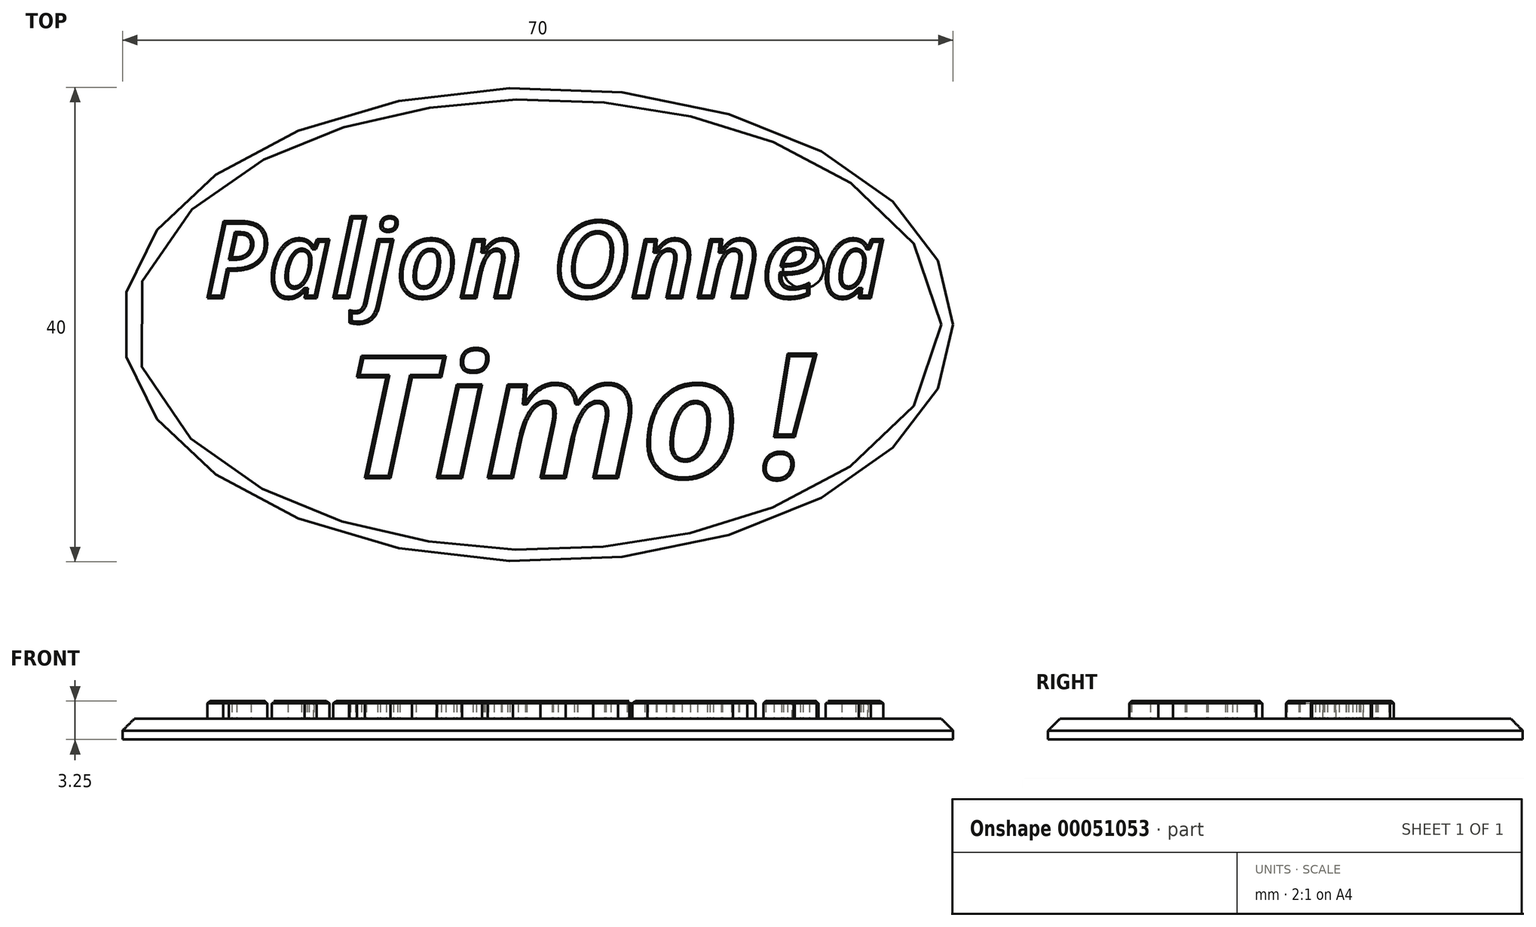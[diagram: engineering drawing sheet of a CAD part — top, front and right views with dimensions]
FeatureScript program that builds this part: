
annotation { "Feature Type Name" : "Feature", "Feature Type Description" : "" }
export const myFeature = defineFeature(function(context is Context, id is Id, definition is map)
    precondition{}
    {
        {
            var Q0;
            Q0=qCreatedBy(makeId("Top.planeOp"),FACE);
            var sketch = newSketch(context, id + "F0", { "sketchPlane" : qUnion([Q0])});
            skEllipse(sketch, "E0", {"center": v(0, 0) * mm, "majorRadius": 35 * mm, "minorRadius": 20 * mm, "majorAxis": v(1, 0)});
            skSolve(sketch);
        }
        {
            var Q0;
            Q0=makeQuery(id+"F0.imprint","IMPRINT",FACE,{"disambiguationData":[TD([[makeQuery(id+"F0.imprint","IMPRINT",EDGE,{"derivedFrom":sQuery(id+"F0.wireOp",EDGE,"E0")}),1.0]])]});
            extrude(context, id + "F1", {"entities" : qUnion([Q0]), "depth" : 1.75 * mm});
        }
        {
            var Q0;
            Q0=makeQuery(id+"F1.opExtrude","CAP_FACE",FACE,{"disambiguationData":[OSD([sQuery(id+"F0.wireOp",EDGE,"E0")])],"isStart":false});
            var sketch = newSketch(context, id + "F2", { "sketchPlane" : qUnion([Q0])});
            skText(sketch, "E1", { "text": "Paljon Onnea ", "fontName": "OpenSans-BoldItalic.ttf"});
            const initialGuessF2  = {"E1": [-0.0281, 0.00223, 1, 0, 0.00655]};
            skSetInitialGuess(sketch, initialGuessF2);
            skSolve(sketch);
        }
        {
            var Q0;
            Q0=makeQuery(id+"F2.imprint","IMPRINT",FACE,{"disambiguationData":[TD([[makeQuery(id+"F2.imprint","IMPRINT",EDGE,{"derivedFrom":sQuery(id+"F2.wireOp",EDGE,"E1.sketch_text.stroke-6")}),1.0]])]});
            var sketch = newSketch(context, id + "F3", { "sketchPlane" : qUnion([Q0])});
            skText(sketch, "E2", { "text": "Timo", "fontName": "OpenSans-BoldItalic.ttf"});
            const initialGuessF3  = {"E2": [-0.01644, -0.01295, 1, 0, 0.01041]};
            skSetInitialGuess(sketch, initialGuessF3);
            skSolve(sketch);
        }
        {
            var Q0;
            Q0 = qSketchRegion(id + "F2", true);
            var Q1;
            Q1 = qSketchRegion(id + "F3", true);
            extrude(context, id + "F4", {"entities" : qUnion([Q0, Q1]), "operationType" : NewBodyOperationType.ADD, "depth" : 1.5 * mm});
        }
        {
            var Q0;
            Q0=makeQuery(id+"F4.opExtrude","CAP_FACE",FACE,{"disambiguationData":[OSD([sQuery(id+"F3.wireOp",EDGE,"E2.sketch_text.stroke-0"),sQuery(id+"F3.wireOp",EDGE,"E2.sketch_text.stroke-1"),sQuery(id+"F3.wireOp",EDGE,"E2.sketch_text.stroke-2"),sQuery(id+"F3.wireOp",EDGE,"E2.sketch_text.stroke-3"),sQuery(id+"F3.wireOp",EDGE,"E2.sketch_text.stroke-4"),sQuery(id+"F3.wireOp",EDGE,"E2.sketch_text.stroke-5"),sQuery(id+"F3.wireOp",EDGE,"E2.sketch_text.stroke-6"),sQuery(id+"F3.wireOp",EDGE,"E2.sketch_text.stroke-7")])],"isStart":false});
            var Q1;
            Q1=makeQuery(id+"F4.opExtrude","CAP_FACE",FACE,{"disambiguationData":[OSD([sQuery(id+"F3.wireOp",EDGE,"E2.sketch_text.stroke-15"),sQuery(id+"F3.wireOp",EDGE,"E2.sketch_text.stroke-16"),sQuery(id+"F3.wireOp",EDGE,"E2.sketch_text.stroke-17"),sQuery(id+"F3.wireOp",EDGE,"E2.sketch_text.stroke-18")])],"isStart":false});
            var Q2;
            Q2=makeQuery(id+"F4.opExtrude","CAP_FACE",FACE,{"disambiguationData":[OSD([sQuery(id+"F3.wireOp",EDGE,"E2.sketch_text.stroke-8"),sQuery(id+"F3.wireOp",EDGE,"E2.sketch_text.stroke-9"),sQuery(id+"F3.wireOp",EDGE,"E2.sketch_text.stroke-10"),sQuery(id+"F3.wireOp",EDGE,"E2.sketch_text.stroke-11"),sQuery(id+"F3.wireOp",EDGE,"E2.sketch_text.stroke-12"),sQuery(id+"F3.wireOp",EDGE,"E2.sketch_text.stroke-13"),sQuery(id+"F3.wireOp",EDGE,"E2.sketch_text.stroke-14")])],"isStart":false});
            var Q3;
            Q3=makeQuery(id+"F4.opExtrude","CAP_FACE",FACE,{"disambiguationData":[OSD([sQuery(id+"F3.wireOp",EDGE,"E2.sketch_text.stroke-47"),sQuery(id+"F3.wireOp",EDGE,"E2.sketch_text.stroke-48"),sQuery(id+"F3.wireOp",EDGE,"E2.sketch_text.stroke-49"),sQuery(id+"F3.wireOp",EDGE,"E2.sketch_text.stroke-50"),sQuery(id+"F3.wireOp",EDGE,"E2.sketch_text.stroke-51"),sQuery(id+"F3.wireOp",EDGE,"E2.sketch_text.stroke-52"),sQuery(id+"F3.wireOp",EDGE,"E2.sketch_text.stroke-53"),sQuery(id+"F3.wireOp",EDGE,"E2.sketch_text.stroke-54"),sQuery(id+"F3.wireOp",EDGE,"E2.sketch_text.stroke-55"),sQuery(id+"F3.wireOp",EDGE,"E2.sketch_text.stroke-56"),sQuery(id+"F3.wireOp",EDGE,"E2.sketch_text.stroke-57"),sQuery(id+"F3.wireOp",EDGE,"E2.sketch_text.stroke-58"),sQuery(id+"F3.wireOp",EDGE,"E2.sketch_text.stroke-59"),sQuery(id+"F3.wireOp",EDGE,"E2.sketch_text.stroke-60"),sQuery(id+"F3.wireOp",EDGE,"E2.sketch_text.stroke-61"),sQuery(id+"F3.wireOp",EDGE,"E2.sketch_text.stroke-62"),sQuery(id+"F3.wireOp",EDGE,"E2.sketch_text.stroke-63"),sQuery(id+"F3.wireOp",EDGE,"E2.sketch_text.stroke-64")])],"isStart":false});
            var Q4;
            Q4=makeQuery(id+"F4.opExtrude","CAP_FACE",FACE,{"disambiguationData":[OSD([sQuery(id+"F2.wireOp",EDGE,"E1.sketch_text.stroke-94"),sQuery(id+"F2.wireOp",EDGE,"E1.sketch_text.stroke-95"),sQuery(id+"F2.wireOp",EDGE,"E1.sketch_text.stroke-96"),sQuery(id+"F2.wireOp",EDGE,"E1.sketch_text.stroke-97"),sQuery(id+"F2.wireOp",EDGE,"E1.sketch_text.stroke-98"),sQuery(id+"F2.wireOp",EDGE,"E1.sketch_text.stroke-99"),sQuery(id+"F2.wireOp",EDGE,"E1.sketch_text.stroke-100"),sQuery(id+"F2.wireOp",EDGE,"E1.sketch_text.stroke-101"),sQuery(id+"F2.wireOp",EDGE,"E1.sketch_text.stroke-102"),sQuery(id+"F2.wireOp",EDGE,"E1.sketch_text.stroke-103"),sQuery(id+"F2.wireOp",EDGE,"E1.sketch_text.stroke-104"),sQuery(id+"F2.wireOp",EDGE,"E1.sketch_text.stroke-105"),sQuery(id+"F2.wireOp",EDGE,"E1.sketch_text.stroke-106"),sQuery(id+"F2.wireOp",EDGE,"E1.sketch_text.stroke-107"),sQuery(id+"F2.wireOp",EDGE,"E1.sketch_text.stroke-108"),sQuery(id+"F2.wireOp",EDGE,"E1.sketch_text.stroke-109"),sQuery(id+"F2.wireOp",EDGE,"E1.sketch_text.stroke-110"),sQuery(id+"F2.wireOp",EDGE,"E1.sketch_text.stroke-111"),sQuery(id+"F2.wireOp",EDGE,"E1.sketch_text.stroke-112"),sQuery(id+"F2.wireOp",EDGE,"E1.sketch_text.stroke-113")])],"isStart":false});
            var Q5;
            Q5=makeQuery(id+"F4.opExtrude","CAP_FACE",FACE,{"disambiguationData":[OSD([sQuery(id+"F2.wireOp",EDGE,"E1.sketch_text.stroke-40"),sQuery(id+"F2.wireOp",EDGE,"E1.sketch_text.stroke-41"),sQuery(id+"F2.wireOp",EDGE,"E1.sketch_text.stroke-42"),sQuery(id+"F2.wireOp",EDGE,"E1.sketch_text.stroke-43")])],"isStart":false});
            chamfer(context, id + "F5", {"entities" : qUnion([Q0, Q1, Q2, Q3, Q4, Q5]), "width" : 0.2 * mm});
        }
        {
            var Q0;
            Q0=makeQuery(id+"F4.opExtrude","CAP_FACE",FACE,{"disambiguationData":[OSD([sQuery(id+"F2.wireOp",EDGE,"E1.sketch_text.stroke-0"),sQuery(id+"F2.wireOp",EDGE,"E1.sketch_text.stroke-1"),sQuery(id+"F2.wireOp",EDGE,"E1.sketch_text.stroke-2"),sQuery(id+"F2.wireOp",EDGE,"E1.sketch_text.stroke-3"),sQuery(id+"F2.wireOp",EDGE,"E1.sketch_text.stroke-4"),sQuery(id+"F2.wireOp",EDGE,"E1.sketch_text.stroke-5"),sQuery(id+"F2.wireOp",EDGE,"E1.sketch_text.stroke-6"),sQuery(id+"F2.wireOp",EDGE,"E1.sketch_text.stroke-7"),sQuery(id+"F2.wireOp",EDGE,"E1.sketch_text.stroke-8"),sQuery(id+"F2.wireOp",EDGE,"E1.sketch_text.stroke-9"),sQuery(id+"F2.wireOp",EDGE,"E1.sketch_text.stroke-10"),sQuery(id+"F2.wireOp",EDGE,"E1.sketch_text.stroke-11"),sQuery(id+"F2.wireOp",EDGE,"E1.sketch_text.stroke-12"),sQuery(id+"F2.wireOp",EDGE,"E1.sketch_text.stroke-13"),sQuery(id+"F2.wireOp",EDGE,"E1.sketch_text.stroke-14")])],"isStart":false});
            var Q1;
            Q1=makeQuery(id+"F4.opExtrude","CAP_FACE",FACE,{"disambiguationData":[OSD([sQuery(id+"F2.wireOp",EDGE,"E1.sketch_text.stroke-15"),sQuery(id+"F2.wireOp",EDGE,"E1.sketch_text.stroke-16"),sQuery(id+"F2.wireOp",EDGE,"E1.sketch_text.stroke-17"),sQuery(id+"F2.wireOp",EDGE,"E1.sketch_text.stroke-18"),sQuery(id+"F2.wireOp",EDGE,"E1.sketch_text.stroke-19"),sQuery(id+"F2.wireOp",EDGE,"E1.sketch_text.stroke-20"),sQuery(id+"F2.wireOp",EDGE,"E1.sketch_text.stroke-21"),sQuery(id+"F2.wireOp",EDGE,"E1.sketch_text.stroke-22"),sQuery(id+"F2.wireOp",EDGE,"E1.sketch_text.stroke-23"),sQuery(id+"F2.wireOp",EDGE,"E1.sketch_text.stroke-24"),sQuery(id+"F2.wireOp",EDGE,"E1.sketch_text.stroke-25"),sQuery(id+"F2.wireOp",EDGE,"E1.sketch_text.stroke-26"),sQuery(id+"F2.wireOp",EDGE,"E1.sketch_text.stroke-27"),sQuery(id+"F2.wireOp",EDGE,"E1.sketch_text.stroke-28"),sQuery(id+"F2.wireOp",EDGE,"E1.sketch_text.stroke-29"),sQuery(id+"F2.wireOp",EDGE,"E1.sketch_text.stroke-30"),sQuery(id+"F2.wireOp",EDGE,"E1.sketch_text.stroke-31"),sQuery(id+"F2.wireOp",EDGE,"E1.sketch_text.stroke-32"),sQuery(id+"F2.wireOp",EDGE,"E1.sketch_text.stroke-33"),sQuery(id+"F2.wireOp",EDGE,"E1.sketch_text.stroke-34"),sQuery(id+"F2.wireOp",EDGE,"E1.sketch_text.stroke-35"),sQuery(id+"F2.wireOp",EDGE,"E1.sketch_text.stroke-36"),sQuery(id+"F2.wireOp",EDGE,"E1.sketch_text.stroke-37"),sQuery(id+"F2.wireOp",EDGE,"E1.sketch_text.stroke-38"),sQuery(id+"F2.wireOp",EDGE,"E1.sketch_text.stroke-39")])],"isStart":false});
            var Q2;
            Q2=makeQuery(id+"F4.opExtrude","CAP_FACE",FACE,{"disambiguationData":[OSD([sQuery(id+"F2.wireOp",EDGE,"E1.sketch_text.stroke-44"),sQuery(id+"F2.wireOp",EDGE,"E1.sketch_text.stroke-45"),sQuery(id+"F2.wireOp",EDGE,"E1.sketch_text.stroke-46"),sQuery(id+"F2.wireOp",EDGE,"E1.sketch_text.stroke-47"),sQuery(id+"F2.wireOp",EDGE,"E1.sketch_text.stroke-48"),sQuery(id+"F2.wireOp",EDGE,"E1.sketch_text.stroke-49"),sQuery(id+"F2.wireOp",EDGE,"E1.sketch_text.stroke-50"),sQuery(id+"F2.wireOp",EDGE,"E1.sketch_text.stroke-51")])],"isStart":false});
            var Q3;
            Q3=makeQuery(id+"F4.opExtrude","CAP_FACE",FACE,{"disambiguationData":[OSD([sQuery(id+"F2.wireOp",EDGE,"E1.sketch_text.stroke-52"),sQuery(id+"F2.wireOp",EDGE,"E1.sketch_text.stroke-53"),sQuery(id+"F2.wireOp",EDGE,"E1.sketch_text.stroke-54"),sQuery(id+"F2.wireOp",EDGE,"E1.sketch_text.stroke-55"),sQuery(id+"F2.wireOp",EDGE,"E1.sketch_text.stroke-56"),sQuery(id+"F2.wireOp",EDGE,"E1.sketch_text.stroke-57"),sQuery(id+"F2.wireOp",EDGE,"E1.sketch_text.stroke-58")])],"isStart":false});
            var Q4;
            Q4=makeQuery(id+"F4.opExtrude","CAP_FACE",FACE,{"disambiguationData":[OSD([sQuery(id+"F2.wireOp",EDGE,"E1.sketch_text.stroke-59"),sQuery(id+"F2.wireOp",EDGE,"E1.sketch_text.stroke-60"),sQuery(id+"F2.wireOp",EDGE,"E1.sketch_text.stroke-61"),sQuery(id+"F2.wireOp",EDGE,"E1.sketch_text.stroke-62"),sQuery(id+"F2.wireOp",EDGE,"E1.sketch_text.stroke-63"),sQuery(id+"F2.wireOp",EDGE,"E1.sketch_text.stroke-64"),sQuery(id+"F2.wireOp",EDGE,"E1.sketch_text.stroke-65"),sQuery(id+"F2.wireOp",EDGE,"E1.sketch_text.stroke-66"),sQuery(id+"F2.wireOp",EDGE,"E1.sketch_text.stroke-67"),sQuery(id+"F2.wireOp",EDGE,"E1.sketch_text.stroke-68"),sQuery(id+"F2.wireOp",EDGE,"E1.sketch_text.stroke-69"),sQuery(id+"F2.wireOp",EDGE,"E1.sketch_text.stroke-70"),sQuery(id+"F2.wireOp",EDGE,"E1.sketch_text.stroke-71"),sQuery(id+"F2.wireOp",EDGE,"E1.sketch_text.stroke-72"),sQuery(id+"F2.wireOp",EDGE,"E1.sketch_text.stroke-73"),sQuery(id+"F2.wireOp",EDGE,"E1.sketch_text.stroke-74"),sQuery(id+"F2.wireOp",EDGE,"E1.sketch_text.stroke-75"),sQuery(id+"F2.wireOp",EDGE,"E1.sketch_text.stroke-76")])],"isStart":false});
            var Q5;
            Q5=makeQuery(id+"F4.opExtrude","CAP_FACE",FACE,{"disambiguationData":[OSD([sQuery(id+"F2.wireOp",EDGE,"E1.sketch_text.stroke-77"),sQuery(id+"F2.wireOp",EDGE,"E1.sketch_text.stroke-78"),sQuery(id+"F2.wireOp",EDGE,"E1.sketch_text.stroke-79"),sQuery(id+"F2.wireOp",EDGE,"E1.sketch_text.stroke-80"),sQuery(id+"F2.wireOp",EDGE,"E1.sketch_text.stroke-81"),sQuery(id+"F2.wireOp",EDGE,"E1.sketch_text.stroke-82"),sQuery(id+"F2.wireOp",EDGE,"E1.sketch_text.stroke-83"),sQuery(id+"F2.wireOp",EDGE,"E1.sketch_text.stroke-84"),sQuery(id+"F2.wireOp",EDGE,"E1.sketch_text.stroke-85"),sQuery(id+"F2.wireOp",EDGE,"E1.sketch_text.stroke-86"),sQuery(id+"F2.wireOp",EDGE,"E1.sketch_text.stroke-87"),sQuery(id+"F2.wireOp",EDGE,"E1.sketch_text.stroke-88"),sQuery(id+"F2.wireOp",EDGE,"E1.sketch_text.stroke-89"),sQuery(id+"F2.wireOp",EDGE,"E1.sketch_text.stroke-90"),sQuery(id+"F2.wireOp",EDGE,"E1.sketch_text.stroke-91"),sQuery(id+"F2.wireOp",EDGE,"E1.sketch_text.stroke-92"),sQuery(id+"F2.wireOp",EDGE,"E1.sketch_text.stroke-93")])],"isStart":false});
            chamfer(context, id + "F6", {"entities" : qUnion([Q0, Q1, Q2, Q3, Q4, Q5]), "width" : 0.2 * mm});
        }
        {
            var Q0;
            Q0=makeQuery(id+"F4.opExtrude","CAP_FACE",FACE,{"disambiguationData":[OSD([sQuery(id+"F2.wireOp",EDGE,"E1.sketch_text.stroke-114"),sQuery(id+"F2.wireOp",EDGE,"E1.sketch_text.stroke-115"),sQuery(id+"F2.wireOp",EDGE,"E1.sketch_text.stroke-116"),sQuery(id+"F2.wireOp",EDGE,"E1.sketch_text.stroke-117"),sQuery(id+"F2.wireOp",EDGE,"E1.sketch_text.stroke-118"),sQuery(id+"F2.wireOp",EDGE,"E1.sketch_text.stroke-119"),sQuery(id+"F2.wireOp",EDGE,"E1.sketch_text.stroke-120"),sQuery(id+"F2.wireOp",EDGE,"E1.sketch_text.stroke-121"),sQuery(id+"F2.wireOp",EDGE,"E1.sketch_text.stroke-122"),sQuery(id+"F2.wireOp",EDGE,"E1.sketch_text.stroke-123"),sQuery(id+"F2.wireOp",EDGE,"E1.sketch_text.stroke-124"),sQuery(id+"F2.wireOp",EDGE,"E1.sketch_text.stroke-125"),sQuery(id+"F2.wireOp",EDGE,"E1.sketch_text.stroke-126"),sQuery(id+"F2.wireOp",EDGE,"E1.sketch_text.stroke-127"),sQuery(id+"F2.wireOp",EDGE,"E1.sketch_text.stroke-128"),sQuery(id+"F2.wireOp",EDGE,"E1.sketch_text.stroke-129"),sQuery(id+"F2.wireOp",EDGE,"E1.sketch_text.stroke-130")])],"isStart":false});
            var Q1;
            Q1=makeQuery(id+"F4.opExtrude","CAP_FACE",FACE,{"disambiguationData":[OSD([sQuery(id+"F2.wireOp",EDGE,"E1.sketch_text.stroke-131"),sQuery(id+"F2.wireOp",EDGE,"E1.sketch_text.stroke-132"),sQuery(id+"F2.wireOp",EDGE,"E1.sketch_text.stroke-133"),sQuery(id+"F2.wireOp",EDGE,"E1.sketch_text.stroke-134"),sQuery(id+"F2.wireOp",EDGE,"E1.sketch_text.stroke-135"),sQuery(id+"F2.wireOp",EDGE,"E1.sketch_text.stroke-136"),sQuery(id+"F2.wireOp",EDGE,"E1.sketch_text.stroke-137"),sQuery(id+"F2.wireOp",EDGE,"E1.sketch_text.stroke-138"),sQuery(id+"F2.wireOp",EDGE,"E1.sketch_text.stroke-139"),sQuery(id+"F2.wireOp",EDGE,"E1.sketch_text.stroke-140"),sQuery(id+"F2.wireOp",EDGE,"E1.sketch_text.stroke-141"),sQuery(id+"F2.wireOp",EDGE,"E1.sketch_text.stroke-142"),sQuery(id+"F2.wireOp",EDGE,"E1.sketch_text.stroke-143"),sQuery(id+"F2.wireOp",EDGE,"E1.sketch_text.stroke-144"),sQuery(id+"F2.wireOp",EDGE,"E1.sketch_text.stroke-145"),sQuery(id+"F2.wireOp",EDGE,"E1.sketch_text.stroke-146"),sQuery(id+"F2.wireOp",EDGE,"E1.sketch_text.stroke-147")])],"isStart":false});
            var Q2;
            Q2=makeQuery(id+"F4.opExtrude","CAP_FACE",FACE,{"disambiguationData":[OSD([sQuery(id+"F2.wireOp",EDGE,"E1.sketch_text.stroke-148"),sQuery(id+"F2.wireOp",EDGE,"E1.sketch_text.stroke-149"),sQuery(id+"F2.wireOp",EDGE,"E1.sketch_text.stroke-150"),sQuery(id+"F2.wireOp",EDGE,"E1.sketch_text.stroke-151"),sQuery(id+"F2.wireOp",EDGE,"E1.sketch_text.stroke-152"),sQuery(id+"F2.wireOp",EDGE,"E1.sketch_text.stroke-153"),sQuery(id+"F2.wireOp",EDGE,"E1.sketch_text.stroke-154"),sQuery(id+"F2.wireOp",EDGE,"E1.sketch_text.stroke-155"),sQuery(id+"F2.wireOp",EDGE,"E1.sketch_text.stroke-156"),sQuery(id+"F2.wireOp",EDGE,"E1.sketch_text.stroke-157"),sQuery(id+"F2.wireOp",EDGE,"E1.sketch_text.stroke-158"),sQuery(id+"F2.wireOp",EDGE,"E1.sketch_text.stroke-159"),sQuery(id+"F2.wireOp",EDGE,"E1.sketch_text.stroke-160"),sQuery(id+"F2.wireOp",EDGE,"E1.sketch_text.stroke-161"),sQuery(id+"F2.wireOp",EDGE,"E1.sketch_text.stroke-162"),sQuery(id+"F2.wireOp",EDGE,"E1.sketch_text.stroke-163"),sQuery(id+"F2.wireOp",EDGE,"E1.sketch_text.stroke-164"),sQuery(id+"F2.wireOp",EDGE,"E1.sketch_text.stroke-165"),sQuery(id+"F2.wireOp",EDGE,"E1.sketch_text.stroke-166"),sQuery(id+"F2.wireOp",EDGE,"E1.sketch_text.stroke-167"),sQuery(id+"F2.wireOp",EDGE,"E1.sketch_text.stroke-168"),sQuery(id+"F2.wireOp",EDGE,"E1.sketch_text.stroke-169"),sQuery(id+"F2.wireOp",EDGE,"E1.sketch_text.stroke-170"),sQuery(id+"F2.wireOp",EDGE,"E1.sketch_text.stroke-171")])],"isStart":false});
            var Q3;
            Q3=makeQuery(id+"F4.opExtrude","CAP_FACE",FACE,{"disambiguationData":[OSD([sQuery(id+"F2.wireOp",EDGE,"E1.sketch_text.stroke-172"),sQuery(id+"F2.wireOp",EDGE,"E1.sketch_text.stroke-173"),sQuery(id+"F2.wireOp",EDGE,"E1.sketch_text.stroke-174"),sQuery(id+"F2.wireOp",EDGE,"E1.sketch_text.stroke-175"),sQuery(id+"F2.wireOp",EDGE,"E1.sketch_text.stroke-176"),sQuery(id+"F2.wireOp",EDGE,"E1.sketch_text.stroke-177"),sQuery(id+"F2.wireOp",EDGE,"E1.sketch_text.stroke-178"),sQuery(id+"F2.wireOp",EDGE,"E1.sketch_text.stroke-179"),sQuery(id+"F2.wireOp",EDGE,"E1.sketch_text.stroke-180"),sQuery(id+"F2.wireOp",EDGE,"E1.sketch_text.stroke-181"),sQuery(id+"F2.wireOp",EDGE,"E1.sketch_text.stroke-182"),sQuery(id+"F2.wireOp",EDGE,"E1.sketch_text.stroke-183"),sQuery(id+"F2.wireOp",EDGE,"E1.sketch_text.stroke-184"),sQuery(id+"F2.wireOp",EDGE,"E1.sketch_text.stroke-185"),sQuery(id+"F2.wireOp",EDGE,"E1.sketch_text.stroke-186"),sQuery(id+"F2.wireOp",EDGE,"E1.sketch_text.stroke-187"),sQuery(id+"F2.wireOp",EDGE,"E1.sketch_text.stroke-188"),sQuery(id+"F2.wireOp",EDGE,"E1.sketch_text.stroke-189"),sQuery(id+"F2.wireOp",EDGE,"E1.sketch_text.stroke-190"),sQuery(id+"F2.wireOp",EDGE,"E1.sketch_text.stroke-191"),sQuery(id+"F2.wireOp",EDGE,"E1.sketch_text.stroke-192"),sQuery(id+"F2.wireOp",EDGE,"E1.sketch_text.stroke-193"),sQuery(id+"F2.wireOp",EDGE,"E1.sketch_text.stroke-194"),sQuery(id+"F2.wireOp",EDGE,"E1.sketch_text.stroke-195"),sQuery(id+"F2.wireOp",EDGE,"E1.sketch_text.stroke-196")])],"isStart":false});
            var Q4;
            Q4=makeQuery(id+"F4.opExtrude","CAP_FACE",FACE,{"disambiguationData":[OSD([sQuery(id+"F3.wireOp",EDGE,"E2.sketch_text.stroke-19"),sQuery(id+"F3.wireOp",EDGE,"E2.sketch_text.stroke-20"),sQuery(id+"F3.wireOp",EDGE,"E2.sketch_text.stroke-21"),sQuery(id+"F3.wireOp",EDGE,"E2.sketch_text.stroke-22"),sQuery(id+"F3.wireOp",EDGE,"E2.sketch_text.stroke-23"),sQuery(id+"F3.wireOp",EDGE,"E2.sketch_text.stroke-24"),sQuery(id+"F3.wireOp",EDGE,"E2.sketch_text.stroke-25"),sQuery(id+"F3.wireOp",EDGE,"E2.sketch_text.stroke-26"),sQuery(id+"F3.wireOp",EDGE,"E2.sketch_text.stroke-27"),sQuery(id+"F3.wireOp",EDGE,"E2.sketch_text.stroke-28"),sQuery(id+"F3.wireOp",EDGE,"E2.sketch_text.stroke-29"),sQuery(id+"F3.wireOp",EDGE,"E2.sketch_text.stroke-30"),sQuery(id+"F3.wireOp",EDGE,"E2.sketch_text.stroke-31"),sQuery(id+"F3.wireOp",EDGE,"E2.sketch_text.stroke-32"),sQuery(id+"F3.wireOp",EDGE,"E2.sketch_text.stroke-33"),sQuery(id+"F3.wireOp",EDGE,"E2.sketch_text.stroke-34"),sQuery(id+"F3.wireOp",EDGE,"E2.sketch_text.stroke-35"),sQuery(id+"F3.wireOp",EDGE,"E2.sketch_text.stroke-36"),sQuery(id+"F3.wireOp",EDGE,"E2.sketch_text.stroke-37"),sQuery(id+"F3.wireOp",EDGE,"E2.sketch_text.stroke-38"),sQuery(id+"F3.wireOp",EDGE,"E2.sketch_text.stroke-39"),sQuery(id+"F3.wireOp",EDGE,"E2.sketch_text.stroke-40"),sQuery(id+"F3.wireOp",EDGE,"E2.sketch_text.stroke-41"),sQuery(id+"F3.wireOp",EDGE,"E2.sketch_text.stroke-42"),sQuery(id+"F3.wireOp",EDGE,"E2.sketch_text.stroke-43"),sQuery(id+"F3.wireOp",EDGE,"E2.sketch_text.stroke-44"),sQuery(id+"F3.wireOp",EDGE,"E2.sketch_text.stroke-45"),sQuery(id+"F3.wireOp",EDGE,"E2.sketch_text.stroke-46")])],"isStart":false});
            chamfer(context, id + "F7", {"entities" : qUnion([Q0, Q1, Q2, Q3, Q4]), "width" : 0.2 * mm});
        }
        {
            var Q0;
            Q0=makeQuery(id+"F2.imprint","IMPRINT",FACE,{"disambiguationData":[TD([[makeQuery(id+"F2.imprint","IMPRINT",EDGE,{"derivedFrom":sQuery(id+"F2.wireOp",EDGE,"E1.sketch_text.stroke-6")}),1.0]])]});
            var sketch = newSketch(context, id + "F8", { "sketchPlane" : qUnion([Q0])});
            skText(sketch, "E3", { "text": "!", "fontName": "OpenSans-BoldItalic.ttf"});
            const initialGuessF8  = {"E3": [0.01883, -0.01297, 1, 0, 0.0106]};
            skSetInitialGuess(sketch, initialGuessF8);
            skSolve(sketch);
        }
        {
            var Q0;
            Q0 = qSketchRegion(id + "F8", true);
            extrude(context, id + "F9", {"entities" : qUnion([Q0]), "operationType" : NewBodyOperationType.ADD, "depth" : 1.5 * mm});
        }
        {
            var Q0;
            Q0=makeQuery(id+"F1.opExtrude","CAP_EDGE",EDGE,{"disambiguationData":[OSD([sQuery(id+"F0.wireOp",EDGE,"E0")])],"isStart":false});
            chamfer(context, id + "F10", {"entities" : qUnion([Q0]), "width" : 1 * mm, "tangentPropagation" : true});
        }
        {
            var Q0;
            Q0=makeQuery(id+"F9.opExtrude","CAP_FACE",FACE,{"disambiguationData":[OSD([sQuery(id+"F8.wireOp",EDGE,"E3.sketch_text.stroke-0"),sQuery(id+"F8.wireOp",EDGE,"E3.sketch_text.stroke-1"),sQuery(id+"F8.wireOp",EDGE,"E3.sketch_text.stroke-2"),sQuery(id+"F8.wireOp",EDGE,"E3.sketch_text.stroke-3")])],"isStart":false});
            var Q1;
            Q1=makeQuery(id+"F9.opExtrude","CAP_FACE",FACE,{"disambiguationData":[OSD([sQuery(id+"F8.wireOp",EDGE,"E3.sketch_text.stroke-4"),sQuery(id+"F8.wireOp",EDGE,"E3.sketch_text.stroke-5"),sQuery(id+"F8.wireOp",EDGE,"E3.sketch_text.stroke-6"),sQuery(id+"F8.wireOp",EDGE,"E3.sketch_text.stroke-7"),sQuery(id+"F8.wireOp",EDGE,"E3.sketch_text.stroke-8"),sQuery(id+"F8.wireOp",EDGE,"E3.sketch_text.stroke-9"),sQuery(id+"F8.wireOp",EDGE,"E3.sketch_text.stroke-10"),sQuery(id+"F8.wireOp",EDGE,"E3.sketch_text.stroke-11")])],"isStart":false});
            chamfer(context, id + "F11", {"entities" : qUnion([Q0, Q1]), "width" : 0.2 * mm, "tangentPropagation" : true});
        }
    });
